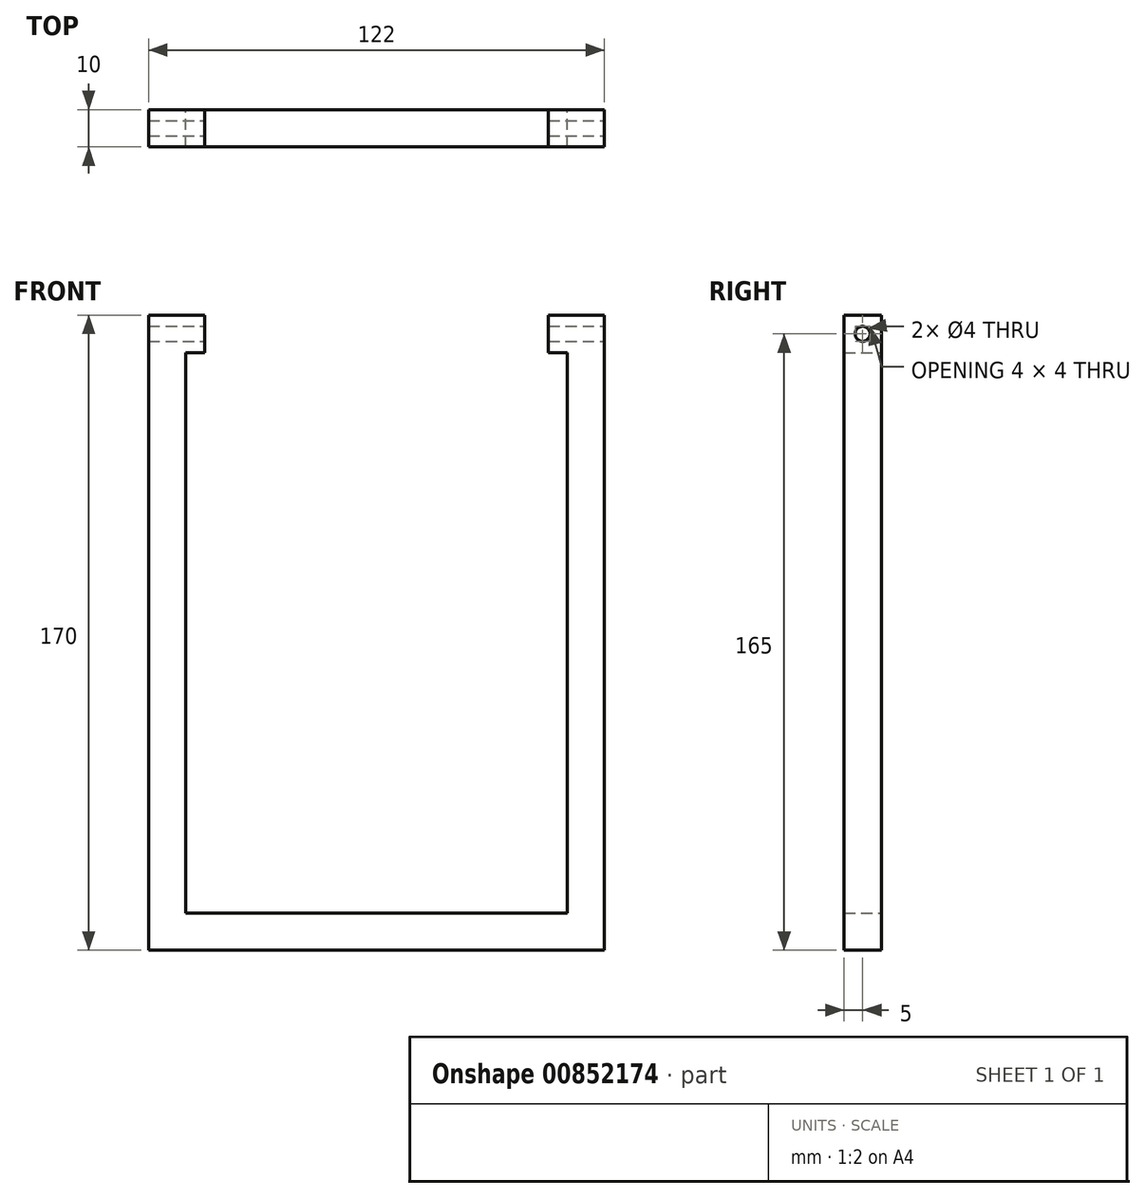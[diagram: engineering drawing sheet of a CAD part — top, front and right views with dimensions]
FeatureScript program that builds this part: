
annotation { "Feature Type Name" : "Feature", "Feature Type Description" : "" }
export const myFeature = defineFeature(function(context is Context, id is Id, definition is map)
    precondition{}
    {
        {
            var Q0;
            Q0=qCreatedBy(makeId("Front.planeOp"),FACE);
            var sketch = newSketch(context, id + "F0", { "sketchPlane" : qUnion([Q0])});
            skLineSegment(sketch, "E0", {"start": v(-61, 0) * mm, "end": v(-61, 170) * mm});
            skLineSegment(sketch, "E1", {"start": v(-61, 170) * mm, "end": v(-46, 170) * mm});
            skLineSegment(sketch, "E2", {"start": v(-46, 170) * mm, "end": v(-46, 160) * mm});
            skLineSegment(sketch, "E3", {"start": v(-46, 160) * mm, "end": v(-51, 160) * mm});
            skLineSegment(sketch, "E4", {"start": v(-51, 160) * mm, "end": v(-51, 10) * mm});
            skLineSegment(sketch, "E5", {"start": v(-51, 10) * mm, "end": v(0, 10) * mm});
            skLineSegment(sketch, "E6.MirrorCS", {"start": v(61, 0) * mm, "end": v(61, 170) * mm});
            skLineSegment(sketch, "E7.MirrorCS", {"start": v(61, 170) * mm, "end": v(46, 170) * mm});
            skLineSegment(sketch, "E8.MirrorCS", {"start": v(51, 10) * mm, "end": v(0, 10) * mm});
            skLineSegment(sketch, "E9.MirrorCS", {"start": v(46, 170) * mm, "end": v(46, 160) * mm});
            skLineSegment(sketch, "E10.MirrorCS", {"start": v(51, 160) * mm, "end": v(51, 10) * mm});
            skLineSegment(sketch, "E11.MirrorCS", {"start": v(46, 160) * mm, "end": v(51, 160) * mm});
            skLineSegment(sketch, "E12", {"start": v(61, 0) * mm, "end": v(-61, 0) * mm});
            skLineSegment(sketch, "E13", {"start": v(-51, 10) * mm, "end": v(-61, 10) * mm, "construction": true});
            skLineSegment(sketch, "E14", {"start": v(0, 10) * mm, "end": v(0, 0) * mm, "construction": true});
            skSolve(sketch);
        }
        {
            var Q0;
            Q0 = qSketchRegion(id + "F0", true);
            extrude(context, id + "F1", {"entities" : qUnion([Q0]), "depth" : 10 * mm, "offsetDistance" : 25 * mm});
        }
        {
            var Q0;
            Q0=makeQuery(id+"F1.opExtrude","SWEPT_FACE",FACE,{"disambiguationData":[OSD([sQuery(id+"F0.wireOp",EDGE,"E2")])]});
            var sketch = newSketch(context, id + "F2", { "sketchPlane" : qUnion([Q0])});
            skLineSegment(sketch, "E15", {"start": v(-10, 160) * mm, "end": v(0, 170) * mm, "construction": true});
            skCircle(sketch, "E16", {"center": v(-5, 165) * mm, "radius": 2 * mm});
            skSolve(sketch);
        }
        {
            var Q0;
            Q0 = qSketchRegion(id + "F2", true);
            extrude(context, id + "F3", {"entities" : qUnion([Q0]), "operationType" : NewBodyOperationType.REMOVE, "endBound" : BoundingType.THROUGH_ALL, "oppositeDirection" : true, "depth" : 25 * mm, "offsetDistance" : 25 * mm, "hasSecondDirection" : true, "secondDirectionBound" : SecondDirectionBoundingType.THROUGH_ALL, "secondDirectionOppositeDirection" : false, "secondDirectionDepth" : 25 * mm});
        }
    });
